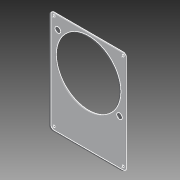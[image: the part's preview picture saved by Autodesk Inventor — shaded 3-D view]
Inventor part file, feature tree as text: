
AUTODESK INVENTOR PART (.ipt)
format: ipt  version: 2014 (Build 180170000, 170)  size: 158,208 bytes
history: native  units: mm
features: extrude x5, sketch x5, other x1, fillet x1, projected_geometry x1
ambient origin geometry x8: Origin, YZ Plane, XZ Plane, XY Plane, X Axis, Y Axis, Z Axis, Center Point
bodies: Body1 (feature_tree)
feature tree (13):
  other  "ソリッド1"
  extrude  "押し出し1"  Depth=92.0mm
  fillet  "フィレット1"  Radius=68.0mm
  extrude  "押し出し2"  Depth=3.0mm
  extrude  "押し出し3"  Depth=3.0mm
  extrude  "押し出し6"  Depth=1.8mm
  extrude  "押し出し7"  Depth=1.8mm
  sketch  "スケッチ1"
  sketch  "スケッチ2"
  sketch  "スケッチ3"
  sketch  "スケッチ6"
  sketch  "スケッチ7"
  projected_geometry  "投影ループ2"
